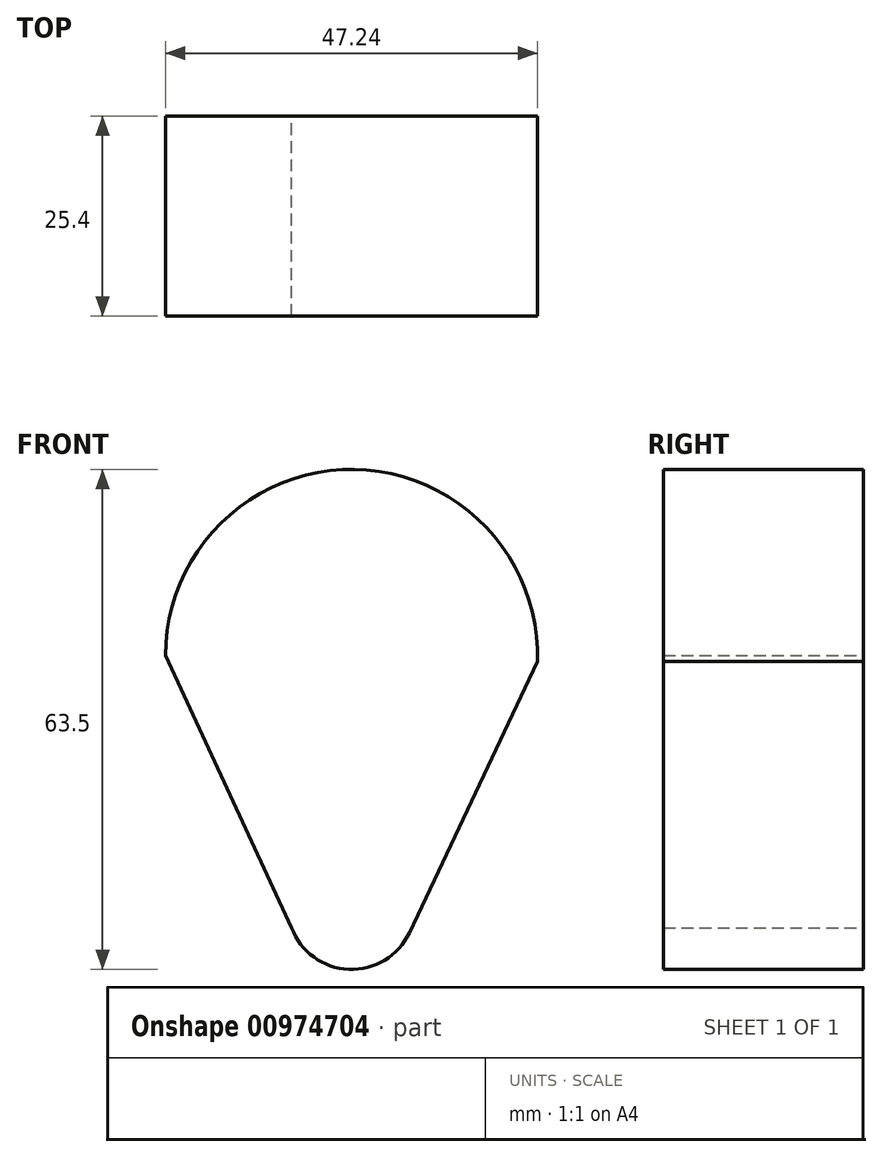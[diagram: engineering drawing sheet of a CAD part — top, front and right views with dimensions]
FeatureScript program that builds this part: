
annotation { "Feature Type Name" : "Feature", "Feature Type Description" : "" }
export const myFeature = defineFeature(function(context is Context, id is Id, definition is map)
    precondition{}
    {
        {
            var Q0;
            Q0=qCreatedBy(makeId("Front.planeOp"),FACE);
            var sketch = newSketch(context, id + "F0", { "sketchPlane" : qUnion([Q0])});
            skLineSegment(sketch, "E0", {"start": v(7.35, -3.47) * mm, "end": v(23.61, 30.99) * mm});
            skArc(sketch, "E1", {"start": v(-23.62, 31.75) * mm, "mid": v(0.38, 55.37) * mm, "end": v(23.61, 30.99) * mm});
            skArc(sketch, "E2", {"start": v(7.35, -3.47) * mm, "mid": v(-0.35, -8.12) * mm, "end": v(-7.62, -2.83) * mm});
            skLineSegment(sketch, "E3", {"start": v(-7.62, -2.83) * mm, "end": v(-23.62, 31.75) * mm});
            skSolve(sketch);
        }
        {
            var Q0;
            Q0 = qSketchRegion(id + "F0", true);
            extrude(context, id + "F1", {"entities" : qUnion([Q0]), "depth" : 25.4 * mm, "offsetDistance" : 25.4 * mm});
        }
    });
